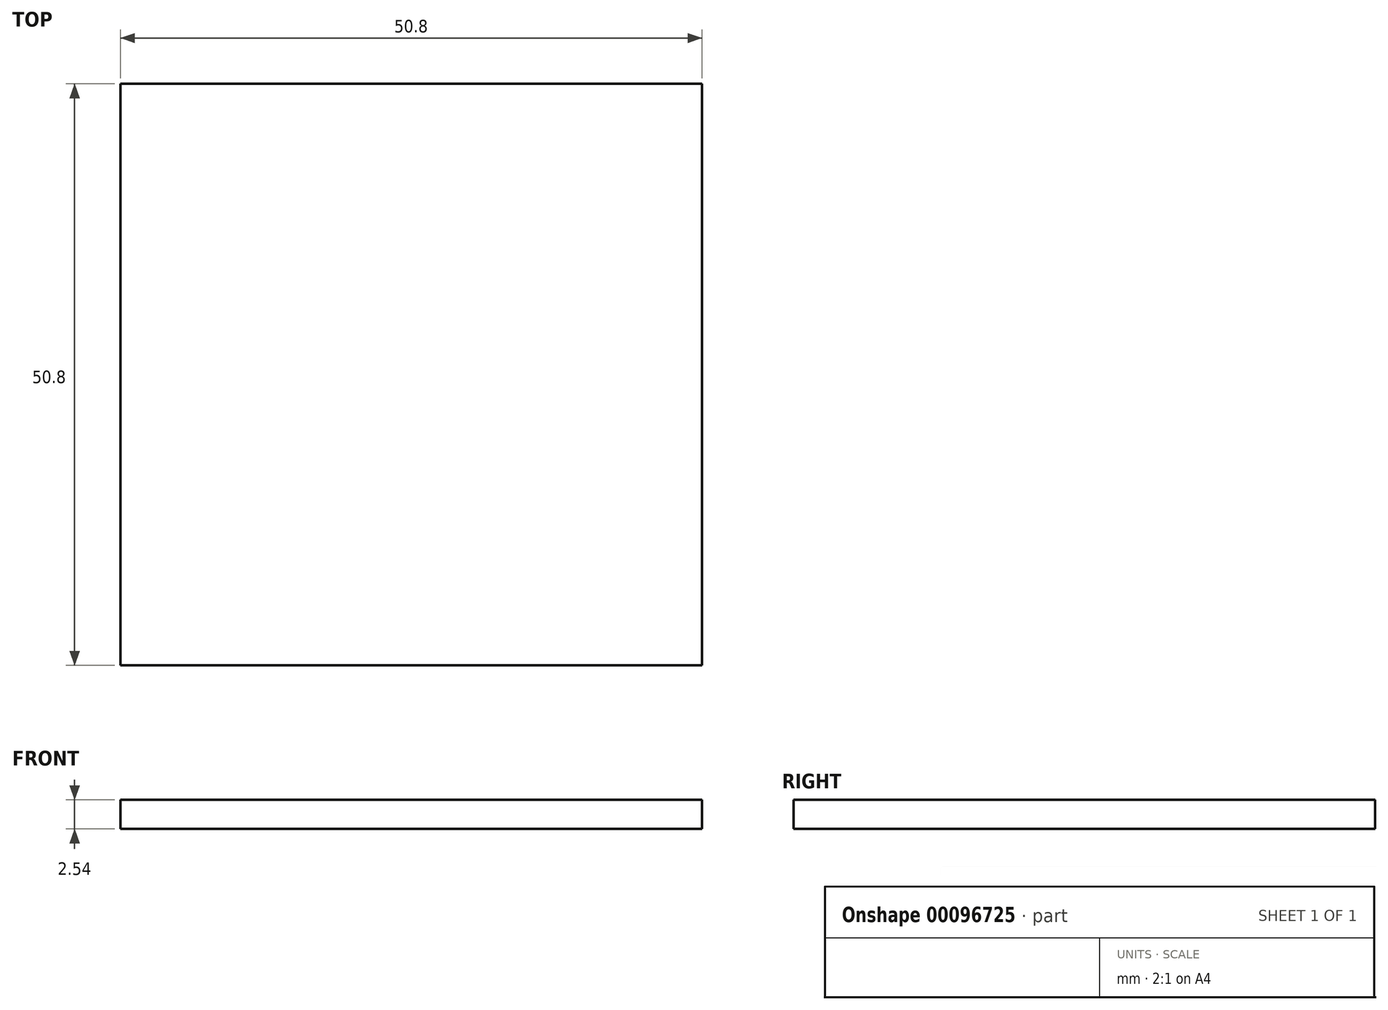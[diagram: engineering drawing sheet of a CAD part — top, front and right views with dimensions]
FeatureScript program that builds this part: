
annotation { "Feature Type Name" : "Feature", "Feature Type Description" : "" }
export const myFeature = defineFeature(function(context is Context, id is Id, definition is map)
    precondition{}
    {
        {
            var Q0;
            Q0=qCreatedBy(makeId("Top.planeOp"),FACE);
            var sketch = newSketch(context, id + "F0", { "sketchPlane" : qUnion([Q0])});
            skLineSegment(sketch, "E0.bottom", {"start": v(-31.08, 37.44) * mm, "end": v(19.72, 37.44) * mm});
            skLineSegment(sketch, "E0.top", {"start": v(-31.08, -13.36) * mm, "end": v(19.72, -13.36) * mm});
            skLineSegment(sketch, "E0.left", {"start": v(-31.08, 37.44) * mm, "end": v(-31.08, -13.36) * mm});
            skLineSegment(sketch, "E0.right", {"start": v(19.72, 37.44) * mm, "end": v(19.72, -13.36) * mm});
            skSolve(sketch);
        }
        {
            var Q0;
            Q0=makeQuery(id+"F0.imprint","IMPRINT",FACE,{"disambiguationData":[TD([[makeQuery(id+"F0.imprint","IMPRINT",EDGE,{"derivedFrom":sQuery(id+"F0.wireOp",EDGE,"E0.bottom")}),-1.0]])]});
            extrude(context, id + "F1", {"entities" : qUnion([Q0]), "depth" : 2.54 * mm});
        }
    });
